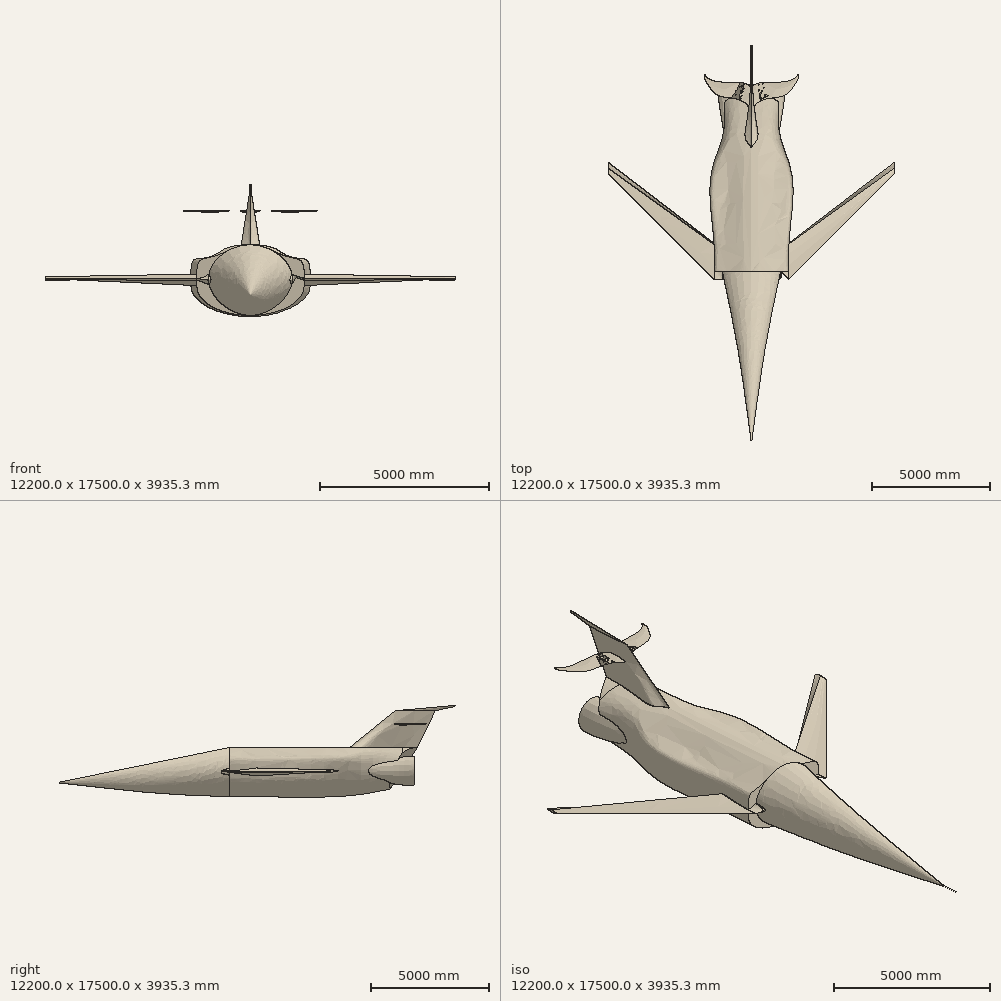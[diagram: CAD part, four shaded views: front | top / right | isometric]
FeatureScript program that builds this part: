
annotation { "Feature Type Name" : "Feature", "Feature Type Description" : "" }
export const myFeature = defineFeature(function(context is Context, id is Id, definition is map)
    precondition{}
    {
        {
            var Q0;
            Q0=qCreatedBy(makeId("Right.planeOp"),FACE);
            var sketch = newSketch(context, id + "F0", { "sketchPlane" : qUnion([Q0])});
            skLineSegment(sketch, "E0", {"start": v(0, 0) * mm, "end": v(-1750, 0) * mm});
            skLineSegment(sketch, "E1", {"start": v(-1750, 0) * mm, "end": v(-3500, 0) * mm});
            skLineSegment(sketch, "E2", {"start": v(-3500, 0) * mm, "end": v(-3500, -1000) * mm});
            skLineSegment(sketch, "E3", {"start": v(-3500, -1000) * mm, "end": v(-8500, -1000) * mm});
            skLineSegment(sketch, "E4", {"start": v(-8500, -1000) * mm, "end": v(-8500, -499.31) * mm});
            skLineSegment(sketch, "E5", {"start": v(-1151.4, 0) * mm, "end": v(-1151.4, 1000) * mm});
            skLineSegment(sketch, "E6", {"start": v(-1151.4, 1000) * mm, "end": v(-8500, -499.31) * mm});
            skLineSegment(sketch, "E7", {"start": v(-8500, -499.31) * mm, "end": v(-3500, -1000) * mm});
            skLineSegment(sketch, "E8", {"start": v(-3500, 0) * mm, "end": v(-3500, 520.82) * mm});
            skLineSegment(sketch, "E9", {"start": v(-8500, -499.31) * mm, "end": v(-8450, -499.31) * mm});
            skLineSegment(sketch, "E10", {"start": v(-8450, -499.31) * mm, "end": v(-8450, -489.1) * mm});
            skLineSegment(sketch, "E11", {"start": v(-8450, -499.31) * mm, "end": v(-8450, -504.32) * mm});
            skSolve(sketch);
        }
        {
            var Q0;
            Q0=sQuery(id+"F0.wireOp",EDGE,"E5");
            cPlane(context, id + "F1", {"entities" : qUnion([Q0]), "cplaneType" : CPlaneType.LINE_ANGLE, "offset" : 25 * mm, "angle" : 90 * degree, "oppositeDirection" : true, "width" : 150 * mm, "height" : 150 * mm});
        }
        {
            var Q0;
            Q0=qCreatedBy(id+"F1.planeOp",FACE);
            var sketch = newSketch(context, id + "F2", { "sketchPlane" : qUnion([Q0])});
            skPoint(sketch, "E12.middle", {"position": v(0, 0) * mm});
            skFitSpline(sketch, "E13", {"points": [v(0, 1000) * mm, v(-1060, 662.5) * mm, v(-1517.6, 506.84) * mm, v(-1600, 0) * mm, v(-1517.6, -506.84) * mm, v(-750, -1000) * mm, v(750, -1000) * mm, v(1517.6, -506.84) * mm, v(1600, 0) * mm, v(1517.6, 506.84) * mm, v(1060, 662.5) * mm, v(0, 1000) * mm]});
            skSolve(sketch);
        }
        {
            var Q0;
            Q0=qCreatedBy(makeId("Front.planeOp"),FACE);
            var sketch = newSketch(context, id + "F3", { "sketchPlane" : qUnion([Q0])});
            skPoint(sketch, "E14.middle", {"position": v(0, 0) * mm});
            skFitSpline(sketch, "E15", {"points": [v(0, 1000) * mm, v(-1060, 662.5) * mm, v(-1517.6, 506.84) * mm, v(-1600, 0) * mm, v(-1517.6, -506.84) * mm, v(-750, -1000) * mm, v(750, -1000) * mm, v(1517.6, -506.84) * mm, v(1600, 0) * mm, v(1517.6, 506.84) * mm, v(1060, 662.5) * mm, v(0, 1000) * mm]});
            skSolve(sketch);
        }
        {
            var Q0;
            Q0=qCreatedBy(makeId("Front.planeOp"),FACE);
            cPlane(context, id + "F4", {"entities" : qUnion([Q0]), "cplaneType" : CPlaneType.OFFSET, "offset" : 3500 * mm, "oppositeDirection" : true, "width" : 150 * mm, "height" : 150 * mm});
        }
        {
            var Q0;
            Q0=qCreatedBy(id+"F4.planeOp",FACE);
            var sketch = newSketch(context, id + "F5", { "sketchPlane" : qUnion([Q0])});
            skPoint(sketch, "E16.middle", {"position": v(0, 0) * mm});
            skFitSpline(sketch, "E17", {"points": [v(0, 1000) * mm, v(-1060, 662.5) * mm, v(-1517.6, 506.84) * mm, v(-1600, 0) * mm, v(-1517.6, -506.84) * mm, v(-750, -1000) * mm, v(750, -1000) * mm, v(1517.6, -506.84) * mm, v(1600, 0) * mm, v(1517.6, 506.84) * mm, v(1060, 662.5) * mm, v(0, 1000) * mm]});
            skSolve(sketch);
        }
        {
            var Q0;
            Q0=qCreatedBy(makeId("Front.planeOp"),FACE);
            cPlane(context, id + "F6", {"entities" : qUnion([Q0]), "cplaneType" : CPlaneType.OFFSET, "offset" : 4500 * mm, "oppositeDirection" : true, "width" : 150 * mm, "height" : 150 * mm});
        }
        {
            var Q0;
            Q0=qCreatedBy(id+"F6.planeOp",FACE);
            var sketch = newSketch(context, id + "F7", { "sketchPlane" : qUnion([Q0])});
            skPoint(sketch, "E18.middle", {"position": v(0, 0) * mm});
            skFitSpline(sketch, "E19", {"points": [v(0, 1000) * mm, v(-1060, 662.5) * mm, v(-1250, 0) * mm, v(-1060, -662.5) * mm, v(0, -1000) * mm, v(1060, -662.5) * mm, v(1250, 0) * mm, v(1060, 662.5) * mm, v(0, 1000) * mm]});
            skSolve(sketch);
        }
        {
            var Q0;
            Q0=qCreatedBy(makeId("Front.planeOp"),FACE);
            cPlane(context, id + "F8", {"entities" : qUnion([Q0]), "cplaneType" : CPlaneType.OFFSET, "offset" : 6232.05 * mm, "oppositeDirection" : true, "width" : 150 * mm, "height" : 150 * mm});
        }
        {
            var Q0;
            Q0=qCreatedBy(id+"F8.planeOp",FACE);
            var sketch = newSketch(context, id + "F9", { "sketchPlane" : qUnion([Q0])});
            skPoint(sketch, "E20.middle", {"position": v(0, 0) * mm});
            skFitSpline(sketch, "E21", {"points": [v(0, 1000) * mm, v(-1060, 662.5) * mm, v(-1250, 0) * mm, v(-848, -530) * mm, v(848, -530) * mm, v(1250, 0) * mm, v(1060, 662.5) * mm, v(0, 1000) * mm]});
            skSolve(sketch);
        }
        {
            var Q0;
            Q0=makeQuery(id+"F2.imprint","IMPRINT",FACE,{"disambiguationData":[TD([[makeQuery(id+"F2.imprint","IMPRINT",EDGE,{"derivedFrom":sQuery(id+"F2.wireOp",EDGE,"E13")}),1.0]])]});
            var Q1;
            Q1=makeQuery(id+"F3.imprint","IMPRINT",FACE,{"disambiguationData":[TD([[makeQuery(id+"F3.imprint","IMPRINT",EDGE,{"derivedFrom":sQuery(id+"F3.wireOp",EDGE,"E15")}),1.0]])]});
            var Q2;
            Q2=makeQuery(id+"F5.imprint","IMPRINT",FACE,{"disambiguationData":[TD([[makeQuery(id+"F5.imprint","IMPRINT",EDGE,{"derivedFrom":sQuery(id+"F5.wireOp",EDGE,"E17")}),1.0]])]});
            var Q3;
            Q3=makeQuery(id+"F7.imprint","IMPRINT",FACE,{"disambiguationData":[TD([[makeQuery(id+"F7.imprint","IMPRINT",EDGE,{"derivedFrom":sQuery(id+"F7.wireOp",EDGE,"E19")}),1.0]])]});
            var Q4;
            Q4=makeQuery(id+"F9.imprint","IMPRINT",FACE,{"disambiguationData":[TD([[makeQuery(id+"F9.imprint","IMPRINT",EDGE,{"derivedFrom":sQuery(id+"F9.wireOp",EDGE,"E21")}),1.0]])]});
            loft(context, id + "F10", {"sheetProfilesArray" : [{ "sheetProfileEntities" : qUnion([Q0]) }, { "sheetProfileEntities" : qUnion([Q1]) }, { "sheetProfileEntities" : qUnion([Q2]) }, { "sheetProfileEntities" : qUnion([Q3]) }, { "sheetProfileEntities" : qUnion([Q4]) }]});
        }
        {
            var Q0;
            Q0=makeQuery(id+"F10.opLoft","CAP_FACE",FACE,{"disambiguationData":[OSD([makeQuery(id+"F9.imprint","IMPRINT",FACE,{"disambiguationData":[TD([[makeQuery(id+"F9.imprint","IMPRINT",EDGE,{"derivedFrom":sQuery(id+"F9.wireOp",EDGE,"E21")}),1.0]])]})])],"isStart":true});
            extrude(context, id + "F11", {"entities" : qUnion([Q0]), "operationType" : NewBodyOperationType.ADD, "depth" : 649.4 * mm, "offsetDistance" : 25 * mm});
        }
        {
            var Q0;
            Q0=qCreatedBy(makeId("Right.planeOp"),FACE);
            var sketch = newSketch(context, id + "F12", { "sketchPlane" : qUnion([Q0])});
            skLineSegment(sketch, "E22", {"start": v(0, 0) * mm, "end": v(4500, 0) * mm});
            skLineSegment(sketch, "E23", {"start": v(4500, 0) * mm, "end": v(6232.05, 0) * mm});
            skLineSegment(sketch, "E24", {"start": v(4500, 0) * mm, "end": v(4500, 1000) * mm});
            skLineSegment(sketch, "E25", {"start": v(4500, 1000) * mm, "end": v(6881.46, 1000) * mm});
            skLineSegment(sketch, "E26", {"start": v(6881.46, 1000) * mm, "end": v(6881.46, -1000) * mm});
            skLineSegment(sketch, "E27", {"start": v(6881.46, 1000) * mm, "end": v(6232.05, 0) * mm});
            skLineSegment(sketch, "E28", {"start": v(6232.05, 0) * mm, "end": v(5582.64, -1000) * mm});
            skLineSegment(sketch, "E29", {"start": v(5582.64, -1000) * mm, "end": v(6881.46, -1000) * mm});
            skSolve(sketch);
        }
        {
            var Q0;
            Q0=makeQuery(id+"F12.imprint","IMPRINT",FACE,{"disambiguationData":[TD([[makeQuery(id+"F12.imprint","IMPRINT",EDGE,{"derivedFrom":sQuery(id+"F12.wireOp",EDGE,"E26")}),-1.0]])]});
            var Q1;
            Q1=sQuery(id+"F12.wireOp",EDGE,"E25");
            revolve(context, id + "F13", {"operationType" : NewBodyOperationType.REMOVE, "entities" : qUnion([Q0]), "axis" : qUnion([Q1]), "revolveType" : RevolveType.SYMMETRIC, "oppositeDirection" : true, "angle" : 182 * degree});
        }
        {
            var Q0;
            Q0=qCreatedBy(id+"F1.planeOp",FACE);
            var sketch = newSketch(context, id + "F14", { "sketchPlane" : qUnion([Q0])});
            skFitSpline(sketch, "E30", {"points": [v(0, 1000) * mm, v(-1250, 0) * mm, v(0, -1099.92) * mm, v(1250, 0) * mm, v(0, 1000) * mm]});
            skSolve(sketch);
        }
        {
            var Q0;
            Q0=qCreatedBy(makeId("Front.planeOp"),FACE);
            cPlane(context, id + "F15", {"entities" : qUnion([Q0]), "cplaneType" : CPlaneType.OFFSET, "offset" : 3500 * mm, "width" : 150 * mm, "height" : 150 * mm});
        }
        {
            var Q0;
            Q0=qCreatedBy(id+"F15.planeOp",FACE);
            var sketch = newSketch(context, id + "F16", { "sketchPlane" : qUnion([Q0])});
            skCircle(sketch, "E31", {"center": v(0, -239.59) * mm, "radius": 760.41 * mm});
            skSolve(sketch);
        }
        {
            var Q0;
            Q0=qCreatedBy(makeId("Front.planeOp"),FACE);
            cPlane(context, id + "F17", {"entities" : qUnion([Q0]), "cplaneType" : CPlaneType.OFFSET, "offset" : 8450 * mm, "width" : 150 * mm, "height" : 150 * mm});
        }
        {
            var Q0;
            Q0=qCreatedBy(id+"F17.planeOp",FACE);
            var sketch = newSketch(context, id + "F18", { "sketchPlane" : qUnion([Q0])});
            skCircle(sketch, "E32", {"center": v(0, -496.71) * mm, "radius": 7.6 * mm});
            skSolve(sketch);
        }
        {
            var Q1;
            Q1=makeQuery(id+"F18.imprint","IMPRINT",FACE,{"disambiguationData":[TD([[makeQuery(id+"F18.imprint","IMPRINT",EDGE,{"derivedFrom":sQuery(id+"F18.wireOp",EDGE,"E32")}),1.0]])]});
            var Q2;
            Q2=makeQuery(id+"F16.imprint","IMPRINT",FACE,{"disambiguationData":[TD([[makeQuery(id+"F16.imprint","IMPRINT",EDGE,{"derivedFrom":sQuery(id+"F16.wireOp",EDGE,"E31")}),1.0]])]});
            var Q3;
            Q3=makeQuery(id+"F14.imprint","IMPRINT",FACE,{"disambiguationData":[TD([[makeQuery(id+"F14.imprint","IMPRINT",EDGE,{"derivedFrom":sQuery(id+"F14.wireOp",EDGE,"E30")}),1.0]])]});
            loft(context, id + "F19", {"operationType" : NewBodyOperationType.ADD, "sheetProfilesArray" : [{ "sheetProfileEntities" : qUnion([Q1]) }, { "sheetProfileEntities" : qUnion([Q2]) }, { "sheetProfileEntities" : qUnion([Q3]) }]});
        }
        {
            var Q0;
            Q0=makeQuery(id+"F19.opLoft","CAP_FACE",FACE,{"disambiguationData":[OSD([makeQuery(id+"F18.imprint","IMPRINT",FACE,{"disambiguationData":[TD([[makeQuery(id+"F18.imprint","IMPRINT",EDGE,{"derivedFrom":sQuery(id+"F18.wireOp",EDGE,"E32")}),1.0]])]})])],"isStart":true});
            extrude(context, id + "F20", {"entities" : qUnion([Q0]), "operationType" : NewBodyOperationType.ADD, "depth" : 550 * mm, "offsetDistance" : 25 * mm});
        }
        {
            var Q0;
            Q0=qCreatedBy(makeId("Front.planeOp"),FACE);
            cPlane(context, id + "F21", {"entities" : qUnion([Q0]), "cplaneType" : CPlaneType.OFFSET, "offset" : 3500 * mm, "oppositeDirection" : true, "width" : 150 * mm, "height" : 150 * mm});
        }
        {
            var Q0;
            Q0=qCreatedBy(id+"F21.planeOp",FACE);
            var sketch = newSketch(context, id + "F22", { "sketchPlane" : qUnion([Q0])});
            skCircle(sketch, "E33", {"center": v(-800, 0) * mm, "radius": 600 * mm});
            skCircle(sketch, "E34", {"center": v(800, 0) * mm, "radius": 600 * mm});
            skSolve(sketch);
        }
        {
            var Q0;
            Q0=qCreatedBy(makeId("Front.planeOp"),FACE);
            cPlane(context, id + "F23", {"entities" : qUnion([Q0]), "cplaneType" : CPlaneType.OFFSET, "offset" : 4500 * mm, "oppositeDirection" : true, "width" : 150 * mm, "height" : 150 * mm});
        }
        {
            var Q0;
            Q0=qCreatedBy(id+"F23.planeOp",FACE);
            var sketch = newSketch(context, id + "F24", { "sketchPlane" : qUnion([Q0])});
            skCircle(sketch, "E35", {"center": v(-800, 0) * mm, "radius": 400 * mm});
            skCircle(sketch, "E36", {"center": v(800, 0) * mm, "radius": 400 * mm});
            skSolve(sketch);
        }
        {
            var Q0;
            Q0=qCreatedBy(makeId("Front.planeOp"),FACE);
            cPlane(context, id + "F25", {"entities" : qUnion([Q0]), "cplaneType" : CPlaneType.OFFSET, "offset" : 6232.05 * mm, "oppositeDirection" : true, "width" : 150 * mm, "height" : 150 * mm});
        }
        {
            var Q0;
            Q0=qCreatedBy(id+"F25.planeOp",FACE);
            var sketch = newSketch(context, id + "F26", { "sketchPlane" : qUnion([Q0])});
            skCircle(sketch, "E37", {"center": v(-800, 0) * mm, "radius": 600 * mm});
            skCircle(sketch, "E38", {"center": v(800, 0) * mm, "radius": 600 * mm});
            skSolve(sketch);
        }
        {
            var Q0;
            Q0=qCreatedBy(makeId("Front.planeOp"),FACE);
            cPlane(context, id + "F27", {"entities" : qUnion([Q0]), "cplaneType" : CPlaneType.OFFSET, "offset" : 6732.05 * mm, "oppositeDirection" : true, "width" : 150 * mm, "height" : 150 * mm});
        }
        {
            var Q0;
            Q0=qCreatedBy(id+"F27.planeOp",FACE);
            var sketch = newSketch(context, id + "F28", { "sketchPlane" : qUnion([Q0])});
            skCircle(sketch, "E39", {"center": v(-800, 0) * mm, "radius": 600 * mm});
            skCircle(sketch, "E40", {"center": v(800, 0) * mm, "radius": 600 * mm});
            skSolve(sketch);
        }
        {
            var Q0;
            Q0=makeQuery(id+"F22.imprint","IMPRINT",FACE,{"disambiguationData":[TD([[makeQuery(id+"F22.imprint","IMPRINT",EDGE,{"derivedFrom":sQuery(id+"F22.wireOp",EDGE,"E33")}),1.0]])]});
            var Q1;
            Q1=makeQuery(id+"F24.imprint","IMPRINT",FACE,{"disambiguationData":[TD([[makeQuery(id+"F24.imprint","IMPRINT",EDGE,{"derivedFrom":sQuery(id+"F24.wireOp",EDGE,"E35")}),1.0]])]});
            var Q2;
            Q2=makeQuery(id+"F26.imprint","IMPRINT",FACE,{"disambiguationData":[TD([[makeQuery(id+"F26.imprint","IMPRINT",EDGE,{"derivedFrom":sQuery(id+"F26.wireOp",EDGE,"E37")}),1.0]])]});
            var Q3;
            Q3=makeQuery(id+"F28.imprint","IMPRINT",FACE,{"disambiguationData":[TD([[makeQuery(id+"F28.imprint","IMPRINT",EDGE,{"derivedFrom":sQuery(id+"F28.wireOp",EDGE,"E39")}),1.0]])]});
            loft(context, id + "F29", {"sheetProfilesArray" : [{ "sheetProfileEntities" : qUnion([Q0]) }, { "sheetProfileEntities" : qUnion([Q1]) }, { "sheetProfileEntities" : qUnion([Q2]) }, { "sheetProfileEntities" : qUnion([Q3]) }]});
        }
        {
            var Q0;
            Q0=makeQuery(id+"F22.imprint","IMPRINT",FACE,{"disambiguationData":[TD([[makeQuery(id+"F22.imprint","IMPRINT",EDGE,{"derivedFrom":sQuery(id+"F22.wireOp",EDGE,"E34")}),1.0]])]});
            var Q1;
            Q1=makeQuery(id+"F24.imprint","IMPRINT",FACE,{"disambiguationData":[TD([[makeQuery(id+"F24.imprint","IMPRINT",EDGE,{"derivedFrom":sQuery(id+"F24.wireOp",EDGE,"E36")}),1.0]])]});
            var Q2;
            Q2=makeQuery(id+"F26.imprint","IMPRINT",FACE,{"disambiguationData":[TD([[makeQuery(id+"F26.imprint","IMPRINT",EDGE,{"derivedFrom":sQuery(id+"F26.wireOp",EDGE,"E38")}),1.0]])]});
            var Q3;
            Q3=makeQuery(id+"F28.imprint","IMPRINT",FACE,{"disambiguationData":[TD([[makeQuery(id+"F28.imprint","IMPRINT",EDGE,{"derivedFrom":sQuery(id+"F28.wireOp",EDGE,"E40")}),1.0]])]});
            loft(context, id + "F30", {"sheetProfilesArray" : [{ "sheetProfileEntities" : qUnion([Q0]) }, { "sheetProfileEntities" : qUnion([Q1]) }, { "sheetProfileEntities" : qUnion([Q2]) }, { "sheetProfileEntities" : qUnion([Q3]) }]});
        }
        {
            var Q0;
            Q0=qCreatedBy(makeId("Right.planeOp"),FACE);
            var sketch = newSketch(context, id + "F31", { "sketchPlane" : qUnion([Q0])});
            skFitSpline(sketch, "E41", {"points": [v(-1500, -50) * mm, v(0, 250) * mm, v(3000, -50) * mm, v(0, -250) * mm, v(-1500, -50) * mm]});
            skSolve(sketch);
        }
        {
            var Q0;
            Q0=qCreatedBy(makeId("Right.planeOp"),FACE);
            cPlane(context, id + "F32", {"entities" : qUnion([Q0]), "cplaneType" : CPlaneType.OFFSET, "offset" : 1600 * mm, "oppositeDirection" : true, "width" : 150 * mm, "height" : 150 * mm});
        }
        {
            var Q0;
            Q0=qCreatedBy(id+"F32.planeOp",FACE);
            var sketch = newSketch(context, id + "F33", { "sketchPlane" : qUnion([Q0])});
            skFitSpline(sketch, "E42", {"points": [v(-1500, 0) * mm, v(1000, 250) * mm, v(3500, 0) * mm], "startDerivative": vector(7500, 0) * mm, "endDerivative": vector(7500, 0) * mm});
            skFitSpline(sketch, "E43", {"points": [v(-1500, 0) * mm, v(1000, -250) * mm, v(3500, 0) * mm], "startDerivative": vector(5000, -750) * mm, "endDerivative": vector(7500, 0) * mm});
            skSolve(sketch);
        }
        {
            var Q0;
            Q0=qCreatedBy(makeId("Right.planeOp"),FACE);
            cPlane(context, id + "F34", {"entities" : qUnion([Q0]), "cplaneType" : CPlaneType.OFFSET, "offset" : 1600 * mm, "width" : 150 * mm, "height" : 150 * mm});
        }
        {
            var Q0;
            Q0=qCreatedBy(id+"F34.planeOp",FACE);
            var sketch = newSketch(context, id + "F35", { "sketchPlane" : qUnion([Q0])});
            skFitSpline(sketch, "E44", {"points": [v(-1500, 0) * mm, v(1000, 250) * mm, v(3500, 0) * mm], "startDerivative": vector(7500, 0) * mm, "endDerivative": vector(7500, 0) * mm});
            skFitSpline(sketch, "E45", {"points": [v(-1500, 0) * mm, v(1000, -250) * mm, v(3500, 0) * mm], "startDerivative": vector(5000, -750) * mm, "endDerivative": vector(7500, 0) * mm});
            skSolve(sketch);
        }
        {
            var Q0;
            Q0=qCreatedBy(makeId("Right.planeOp"),FACE);
            cPlane(context, id + "F36", {"entities" : qUnion([Q0]), "cplaneType" : CPlaneType.OFFSET, "offset" : 6100 * mm, "oppositeDirection" : true, "width" : 150 * mm, "height" : 150 * mm});
        }
        {
            var Q0;
            Q0=qCreatedBy(id+"F36.planeOp",FACE);
            var sketch = newSketch(context, id + "F37", { "sketchPlane" : qUnion([Q0])});
            skFitSpline(sketch, "E46", {"points": [v(3000, 0) * mm, v(3250, 50) * mm, v(3500, 0) * mm], "startDerivative": vector(750, 0) * mm, "endDerivative": vector(750, 0) * mm});
            skFitSpline(sketch, "E47", {"points": [v(3000, 0) * mm, v(3250, -50) * mm, v(3500, 0) * mm], "startDerivative": vector(500, -150) * mm, "endDerivative": vector(750, 0) * mm});
            skSolve(sketch);
        }
        {
            var Q0;
            Q0=qCreatedBy(makeId("Right.planeOp"),FACE);
            cPlane(context, id + "F38", {"entities" : qUnion([Q0]), "cplaneType" : CPlaneType.OFFSET, "offset" : 6100 * mm, "width" : 150 * mm, "height" : 150 * mm});
        }
        {
            var Q0;
            Q0=qCreatedBy(id+"F38.planeOp",FACE);
            var sketch = newSketch(context, id + "F39", { "sketchPlane" : qUnion([Q0])});
            skFitSpline(sketch, "E48", {"points": [v(3000, 0) * mm, v(3250, 50) * mm, v(3500, 0) * mm], "startDerivative": vector(750, 0) * mm, "endDerivative": vector(750, 0) * mm});
            skFitSpline(sketch, "E49", {"points": [v(3000, 0) * mm, v(3250, -50) * mm, v(3500, 0) * mm], "startDerivative": vector(500, -150) * mm, "endDerivative": vector(750, 0) * mm});
            skSolve(sketch);
        }
        {
            var Q0;
            Q0=qSketchRegion(id+"F31",true);
            extrude(context, id + "F40", {"entities" : qUnion([Q0]), "endBound" : BoundingType.SYMMETRIC, "depth" : 2500 * mm, "offsetDistance" : 25 * mm});
        }
        {
            var Q1;
            Q1=makeQuery(id+"F40.opExtrude","CAP_FACE",FACE,{"disambiguationData":[OSD([sQuery(id+"F31.wireOp",EDGE,"E41")])],"isStart":true});
            var Q2;
            {var subQ0=sQuery(id+"F33.wireOp",EDGE,"E42");Q2=makeQuery(id+"F33.imprint","IMPRINT",FACE,{"disambiguationData":[TD([[makeQuery(id+"F33.imprint","IMPRINT",EDGE,{"derivedFrom":subQ0}),-1.0]])]});}
            loft(context, id + "F41", {"operationType" : NewBodyOperationType.ADD, "sheetProfilesArray" : [{ "sheetProfileEntities" : qUnion([Q1]) }, { "sheetProfileEntities" : qUnion([Q2]) }]});
        }
        {
            var Q1;
            Q1=makeQuery(id+"F40.opExtrude","CAP_FACE",FACE,{"disambiguationData":[OSD([sQuery(id+"F31.wireOp",EDGE,"E41")])],"isStart":false});
            var Q2;
            {var subQ0=sQuery(id+"F35.wireOp",EDGE,"E44");Q2=makeQuery(id+"F35.imprint","IMPRINT",FACE,{"disambiguationData":[TD([[makeQuery(id+"F35.imprint","IMPRINT",EDGE,{"derivedFrom":subQ0}),-1.0]])]});}
            loft(context, id + "F42", {"operationType" : NewBodyOperationType.ADD, "sheetProfilesArray" : [{ "sheetProfileEntities" : qUnion([Q1]) }, { "sheetProfileEntities" : qUnion([Q2]) }]});
        }
        {
            var Q1;
            {var subQ0=sQuery(id+"F33.wireOp",EDGE,"E42");Q1=makeQuery(id+"F41.opLoft","CAP_FACE",FACE,{"disambiguationData":[OSD([makeQuery(id+"F33.imprint","IMPRINT",FACE,{"disambiguationData":[TD([[makeQuery(id+"F33.imprint","IMPRINT",EDGE,{"derivedFrom":subQ0}),-1.0]])]})])],"isStart":true});}
            var Q2;
            {var subQ0=sQuery(id+"F37.wireOp",EDGE,"E46");Q2=makeQuery(id+"F37.imprint","IMPRINT",FACE,{"disambiguationData":[TD([[makeQuery(id+"F37.imprint","IMPRINT",EDGE,{"derivedFrom":subQ0}),-1.0]])]});}
            loft(context, id + "F43", {"operationType" : NewBodyOperationType.ADD, "sheetProfilesArray" : [{ "sheetProfileEntities" : qUnion([Q1]) }, { "sheetProfileEntities" : qUnion([Q2]) }]});
        }
        {
            var Q1;
            {var subQ0=sQuery(id+"F35.wireOp",EDGE,"E44");Q1=makeQuery(id+"F42.opLoft","CAP_FACE",FACE,{"disambiguationData":[OSD([makeQuery(id+"F35.imprint","IMPRINT",FACE,{"disambiguationData":[TD([[makeQuery(id+"F35.imprint","IMPRINT",EDGE,{"derivedFrom":subQ0}),-1.0]])]})])],"isStart":true});}
            var Q2;
            {var subQ0=sQuery(id+"F39.wireOp",EDGE,"E48");Q2=makeQuery(id+"F39.imprint","IMPRINT",FACE,{"disambiguationData":[TD([[makeQuery(id+"F39.imprint","IMPRINT",EDGE,{"derivedFrom":subQ0}),-1.0]])]});}
            loft(context, id + "F44", {"operationType" : NewBodyOperationType.ADD, "sheetProfilesArray" : [{ "sheetProfileEntities" : qUnion([Q1]) }, { "sheetProfileEntities" : qUnion([Q2]) }]});
        }
        {
            var Q0;
            Q0=qCreatedBy(makeId("Right.planeOp"),FACE);
            var sketch = newSketch(context, id + "F45", { "sketchPlane" : qUnion([Q0])});
            skLineSegment(sketch, "E50", {"start": v(0, 0) * mm, "end": v(4500, 0) * mm});
            skLineSegment(sketch, "E51", {"start": v(4500, 0) * mm, "end": v(4500, 1000) * mm});
            skLineSegment(sketch, "E52", {"start": v(4500, 1000) * mm, "end": v(4500, 750) * mm});
            skLineSegment(sketch, "E53", {"start": v(4500, 750) * mm, "end": v(4000, 750) * mm});
            skLineSegment(sketch, "E54", {"start": v(4500, 750) * mm, "end": v(6250, 750) * mm});
            skLineSegment(sketch, "E55", {"start": v(4500, 1000) * mm, "end": v(4000, 1000) * mm});
            skLineSegment(sketch, "E56", {"start": v(4500, 1000) * mm, "end": v(6881.46, 1000) * mm});
            skLineSegment(sketch, "E57", {"start": v(6881.46, 1000) * mm, "end": v(8500, 1000) * mm});
            skLineSegment(sketch, "E58", {"start": v(8500, 1000) * mm, "end": v(8500, 2800) * mm});
            skLineSegment(sketch, "E59", {"start": v(6881.46, 1000) * mm, "end": v(7648.6, 2572.89) * mm});
            skLineSegment(sketch, "E60", {"start": v(7648.6, 2572.89) * mm, "end": v(5943.2, 2572.89) * mm});
            skLineSegment(sketch, "E61", {"start": v(5943.2, 2572.89) * mm, "end": v(4000, 1000) * mm});
            skSolve(sketch);
        }
        {
            var Q0;
            Q0=qCreatedBy(makeId("Top.planeOp"),FACE);
            cPlane(context, id + "F46", {"entities" : qUnion([Q0]), "cplaneType" : CPlaneType.OFFSET, "offset" : 750 * mm, "width" : 150 * mm, "height" : 150 * mm});
        }
        {
            var Q0;
            Q0=qCreatedBy(id+"F46.planeOp",FACE);
            var sketch = newSketch(context, id + "F47", { "sketchPlane" : qUnion([Q0])});
            skFitSpline(sketch, "E62", {"points": [v(0, 4000) * mm, v(-250, 4500) * mm, v(0, 6250) * mm], "startDerivative": vector(-889.86, 1147.1) * mm, "endDerivative": vector(737.87, 3164.53) * mm});
            skFitSpline(sketch, "E63", {"points": [v(0, 4000) * mm, v(250, 4500) * mm, v(0, 6250) * mm], "startDerivative": vector(889.86, 1147.1) * mm, "endDerivative": vector(-737.87, 3164.53) * mm});
            skSolve(sketch);
        }
        {
            var Q0;
            Q0=qCreatedBy(makeId("Top.planeOp"),FACE);
            cPlane(context, id + "F48", {"entities" : qUnion([Q0]), "cplaneType" : CPlaneType.OFFSET, "offset" : 1000 * mm, "width" : 150 * mm, "height" : 150 * mm});
        }
        {
            var Q0;
            Q0=qCreatedBy(id+"F48.planeOp",FACE);
            var sketch = newSketch(context, id + "F49", { "sketchPlane" : qUnion([Q0])});
            skFitSpline(sketch, "E64", {"points": [v(0, 4000) * mm, v(-250, 4500) * mm, v(0, 6881.46) * mm], "startDerivative": vector(0, 2302.24) * mm, "endDerivative": vector(0, 5298.17) * mm});
            skFitSpline(sketch, "E65", {"points": [v(0, 4000) * mm, v(250, 4500) * mm, v(0, 6881.46) * mm], "startDerivative": vector(0, 2302.24) * mm, "endDerivative": vector(0, 5298.17) * mm});
            skSolve(sketch);
        }
        {
            var Q0;
            Q0=sQuery(id+"F45.wireOp",EDGE,"E60");
            cPlane(context, id + "F50", {"entities" : qUnion([Q0]), "cplaneType" : CPlaneType.LINE_ANGLE, "offset" : 25 * mm, "angle" : 180 * degree, "width" : 150 * mm, "height" : 150 * mm});
        }
        {
            var Q0;
            Q0=qCreatedBy(id+"F50.planeOp",FACE);
            var sketch = newSketch(context, id + "F51", { "sketchPlane" : qUnion([Q0])});
            skFitSpline(sketch, "E66", {"points": [v(0, 5943.2) * mm, v(-25, 6795.9) * mm, v(0, 7648.6) * mm], "startDerivative": vector(-75, 1705.4) * mm, "endDerivative": vector(75, 1705.4) * mm});
            skFitSpline(sketch, "E67", {"points": [v(0, 5943.2) * mm, v(25, 6795.9) * mm, v(0, 7648.6) * mm], "startDerivative": vector(75, 1705.4) * mm, "endDerivative": vector(-75, 1705.4) * mm});
            skSolve(sketch);
        }
        {
            var Q0;
            Q0=qCreatedBy(makeId("Front.planeOp"),FACE);
            cPlane(context, id + "F52", {"entities" : qUnion([Q0]), "cplaneType" : CPlaneType.OFFSET, "offset" : 8500 * mm, "oppositeDirection" : true, "width" : 150 * mm, "height" : 150 * mm});
        }
        {
            var Q0;
            Q0=qCreatedBy(id+"F52.planeOp",FACE);
            var sketch = newSketch(context, id + "F53", { "sketchPlane" : qUnion([Q0])});
            skCircle(sketch, "E68", {"center": v(0, 2775) * mm, "radius": 25 * mm});
            skSolve(sketch);
        }
        {
            var Q0;
            Q0=qCreatedBy(makeId("Right.planeOp"),FACE);
            var sketch = newSketch(context, id + "F54", { "sketchPlane" : qUnion([Q0])});
            skLineSegment(sketch, "E69", {"start": v(5943.2, 2572.89) * mm, "end": v(8500, 2800) * mm});
            skSolve(sketch);
        }
        {
            var Q1;
            Q1=qSketchRegion(id+"F47",true);
            var Q2;
            Q2=qSketchRegion(id+"F49",true);
            loft(context, id + "F55", {"sheetProfilesArray" : [{ "sheetProfileEntities" : qUnion([Q1]) }, { "sheetProfileEntities" : qUnion([Q2]) }]});
        }
        {
            var Q1;
            {var subQ0=sQuery(id+"F49.wireOp",EDGE,"E64");Q1=makeQuery(id+"F55.opLoft","CAP_FACE",FACE,{"disambiguationData":[OSD([makeQuery(id+"F49.imprint","IMPRINT",FACE,{"disambiguationData":[TD([[makeQuery(id+"F49.imprint","IMPRINT",EDGE,{"derivedFrom":subQ0}),-1.0]])]})])],"isStart":true});}
            var Q2;
            Q2=makeQuery(id+"F51.imprint","IMPRINT",FACE,{"disambiguationData":[TD([[makeQuery(id+"F51.imprint","IMPRINT",EDGE,{"derivedFrom":sQuery(id+"F51.wireOp",EDGE,"E66")}),-1.0]])]});
            loft(context, id + "F56", {"operationType" : NewBodyOperationType.ADD, "sheetProfilesArray" : [{ "sheetProfileEntities" : qUnion([Q1]) }, { "sheetProfileEntities" : qUnion([Q2]) }]});
        }
        {
            var Q1;
            Q1=makeQuery(id+"F56.opLoft","CAP_FACE",FACE,{"disambiguationData":[OSD([makeQuery(id+"F51.imprint","IMPRINT",FACE,{"disambiguationData":[TD([[makeQuery(id+"F51.imprint","IMPRINT",EDGE,{"derivedFrom":sQuery(id+"F51.wireOp",EDGE,"E66")}),-1.0]])]})])],"isStart":true});
            var Q2;
            Q2=makeQuery(id+"F53.imprint","IMPRINT",FACE,{"disambiguationData":[TD([[makeQuery(id+"F53.imprint","IMPRINT",EDGE,{"derivedFrom":sQuery(id+"F53.wireOp",EDGE,"E68")}),1.0]])]});
            var Q3;
            Q3=sQuery(id+"F54.wireOp",EDGE,"E69");
            loft(context, id + "F57", {"operationType" : NewBodyOperationType.ADD, "addGuides" : true, "sheetProfilesArray" : [{ "sheetProfileEntities" : qUnion([Q1]) }, { "sheetProfileEntities" : qUnion([Q2]) }], "guidesArray" : [{ "guideEntities" : qUnion([Q3]), "guideDerivativeType" : LoftGuideDerivativeType.DEFAULT, "guideDerivativeMagnitude" : 1 }]});
        }
        {
            var Q0;
            Q0=qCreatedBy(makeId("Top.planeOp"),FACE);
            cPlane(context, id + "F58", {"entities" : qUnion([Q0]), "cplaneType" : CPlaneType.OFFSET, "offset" : 2000 * mm, "width" : 150 * mm, "height" : 150 * mm});
        }
        {
            var Q0;
            Q0=qCreatedBy(id+"F58.planeOp",FACE);
            var sketch = newSketch(context, id + "F59", { "sketchPlane" : qUnion([Q0])});
            skLineSegment(sketch, "E70", {"start": v(0, 0) * mm, "end": v(0, 4500) * mm});
            skLineSegment(sketch, "E71", {"start": v(0, 4500) * mm, "end": v(0, 7369.2) * mm});
            skLineSegment(sketch, "E72", {"start": v(0, 7369.2) * mm, "end": v(0, 5235.43) * mm});
            skLineSegment(sketch, "E73", {"start": v(0, 6302.31) * mm, "end": v(0, 5302.31) * mm});
            skLineSegment(sketch, "E74", {"start": v(0, 6302.31) * mm, "end": v(0, 7302.31) * mm});
            skLineSegment(sketch, "E75", {"start": v(0, 6302.31) * mm, "end": v(0, 6552.31) * mm});
            skLineSegment(sketch, "E76", {"start": v(0, 6302.31) * mm, "end": v(-1200, 6302.31) * mm});
            skLineSegment(sketch, "E77", {"start": v(0, 6302.31) * mm, "end": v(1200, 6302.31) * mm});
            skLineSegment(sketch, "E78", {"start": v(0, 6552.31) * mm, "end": v(-1700, 6552.31) * mm});
            skLineSegment(sketch, "E79", {"start": v(0, 6552.31) * mm, "end": v(1700, 6552.31) * mm});
            skLineSegment(sketch, "E80", {"start": v(0, 7302.31) * mm, "end": v(-2000, 7302.31) * mm});
            skLineSegment(sketch, "E81", {"start": v(0, 7302.31) * mm, "end": v(2000, 7302.31) * mm});
            skLineSegment(sketch, "E82", {"start": v(-2000, 7302.31) * mm, "end": v(-2000, 7052.31) * mm});
            skLineSegment(sketch, "E83", {"start": v(2000, 7302.31) * mm, "end": v(2000, 7052.31) * mm});
            skFitSpline(sketch, "E84", {"points": [v(0, 5302.31) * mm, v(-1200, 6302.31) * mm, v(-2000, 7052.31) * mm], "startDerivative": vector(0, 5513.6) * mm, "endDerivative": vector(-1974.16, 3290.27) * mm});
            skFitSpline(sketch, "E85", {"points": [v(0, 5302.31) * mm, v(1200, 6302.31) * mm, v(2000, 7052.31) * mm], "startDerivative": vector(0, 5513.6) * mm, "endDerivative": vector(1974.16, 3290.27) * mm});
            skFitSpline(sketch, "E86", {"points": [v(0, 6552.31) * mm, v(-2000, 7302.31) * mm], "startDerivative": vector(0, 2250) * mm, "endDerivative": vector(-900, 2250) * mm});
            skFitSpline(sketch, "E87", {"points": [v(0, 6552.31) * mm, v(2000, 7302.31) * mm], "startDerivative": vector(0, 2250) * mm, "endDerivative": vector(900, 2250) * mm});
            skSolve(sketch);
        }
        {
            var Q0;
            Q0=qCreatedBy(makeId("Right.planeOp"),FACE);
            var sketch = newSketch(context, id + "F60", { "sketchPlane" : qUnion([Q0])});
            skFitSpline(sketch, "E88", {"points": [v(5302.31, 2000) * mm, v(5927.31, 2050) * mm, v(6552.31, 2000) * mm], "startDerivative": vector(1250, 150) * mm, "endDerivative": vector(1250, -150) * mm});
            skFitSpline(sketch, "E89", {"points": [v(5302.31, 2000) * mm, v(5927.31, 1950) * mm, v(6552.31, 2000) * mm], "startDerivative": vector(1250, -150) * mm, "endDerivative": vector(1250, 150) * mm});
            skSolve(sketch);
        }
        {
            var Q0;
            Q0=qCreatedBy(makeId("Right.planeOp"),FACE);
            cPlane(context, id + "F61", {"entities" : qUnion([Q0]), "cplaneType" : CPlaneType.OFFSET, "offset" : 2000 * mm, "oppositeDirection" : true, "width" : 150 * mm, "height" : 150 * mm});
        }
        {
            var Q0;
            Q0=qCreatedBy(id+"F61.planeOp",FACE);
            var sketch = newSketch(context, id + "F62", { "sketchPlane" : qUnion([Q0])});
            skFitSpline(sketch, "E90", {"points": [v(7052.31, 2000) * mm, v(7177.31, 2010) * mm, v(7302.31, 2000) * mm], "startDerivative": vector(250, 30) * mm, "endDerivative": vector(250, -30) * mm});
            skFitSpline(sketch, "E91", {"points": [v(7052.31, 2000) * mm, v(7177.31, 1990) * mm, v(7302.31, 2000) * mm], "startDerivative": vector(250, -30) * mm, "endDerivative": vector(250, 30) * mm});
            skSolve(sketch);
        }
        {
            var Q0;
            Q0=qCreatedBy(makeId("Right.planeOp"),FACE);
            cPlane(context, id + "F63", {"entities" : qUnion([Q0]), "cplaneType" : CPlaneType.OFFSET, "offset" : 2000 * mm, "width" : 150 * mm, "height" : 150 * mm});
        }
        {
            var Q0;
            Q0=qCreatedBy(id+"F63.planeOp",FACE);
            var sketch = newSketch(context, id + "F64", { "sketchPlane" : qUnion([Q0])});
            skFitSpline(sketch, "E92", {"points": [v(7052.31, 2000) * mm, v(7177.31, 2010) * mm, v(7302.31, 2000) * mm], "startDerivative": vector(250, 30) * mm, "endDerivative": vector(250, -30) * mm});
            skFitSpline(sketch, "E93", {"points": [v(7052.31, 2000) * mm, v(7177.31, 1990) * mm, v(7302.31, 2000) * mm], "startDerivative": vector(250, -30) * mm, "endDerivative": vector(250, 30) * mm});
            skSolve(sketch);
        }
        {
            var Q1;
            Q1=qSketchRegion(id+"F60",true);
            var Q2;
            Q2=makeQuery(id+"F62.imprint","IMPRINT",FACE,{"disambiguationData":[TD([[makeQuery(id+"F62.imprint","IMPRINT",EDGE,{"derivedFrom":sQuery(id+"F62.wireOp",EDGE,"E90")}),-1.0]])]});
            var Q3;
            Q3=sQuery(id+"F59.wireOp",EDGE,"E84");
            var Q4;
            Q4=sQuery(id+"F59.wireOp",EDGE,"E86");
            loft(context, id + "F65", {"addGuides" : true, "sheetProfilesArray" : [{ "sheetProfileEntities" : qUnion([Q1]) }, { "sheetProfileEntities" : qUnion([Q2]) }], "guidesArray" : [{ "guideEntities" : qUnion([Q3]), "guideDerivativeType" : LoftGuideDerivativeType.DEFAULT, "guideDerivativeMagnitude" : 1 }, { "guideEntities" : qUnion([Q4]), "guideDerivativeType" : LoftGuideDerivativeType.DEFAULT, "guideDerivativeMagnitude" : 1 }]});
        }
        {
            var Q1;
            Q1=qSketchRegion(id+"F60",true);
            var Q2;
            Q2=makeQuery(id+"F64.imprint","IMPRINT",FACE,{"disambiguationData":[TD([[makeQuery(id+"F64.imprint","IMPRINT",EDGE,{"derivedFrom":sQuery(id+"F64.wireOp",EDGE,"E92")}),-1.0]])]});
            var Q3;
            Q3=sQuery(id+"F59.wireOp",EDGE,"E85");
            var Q4;
            Q4=sQuery(id+"F59.wireOp",EDGE,"E87");
            loft(context, id + "F66", {"operationType" : NewBodyOperationType.ADD, "addGuides" : true, "sheetProfilesArray" : [{ "sheetProfileEntities" : qUnion([Q1]) }, { "sheetProfileEntities" : qUnion([Q2]) }], "guidesArray" : [{ "guideEntities" : qUnion([Q3]), "guideDerivativeType" : LoftGuideDerivativeType.DEFAULT, "guideDerivativeMagnitude" : 1 }, { "guideEntities" : qUnion([Q4]), "guideDerivativeType" : LoftGuideDerivativeType.DEFAULT, "guideDerivativeMagnitude" : 1 }]});
        }
    });
